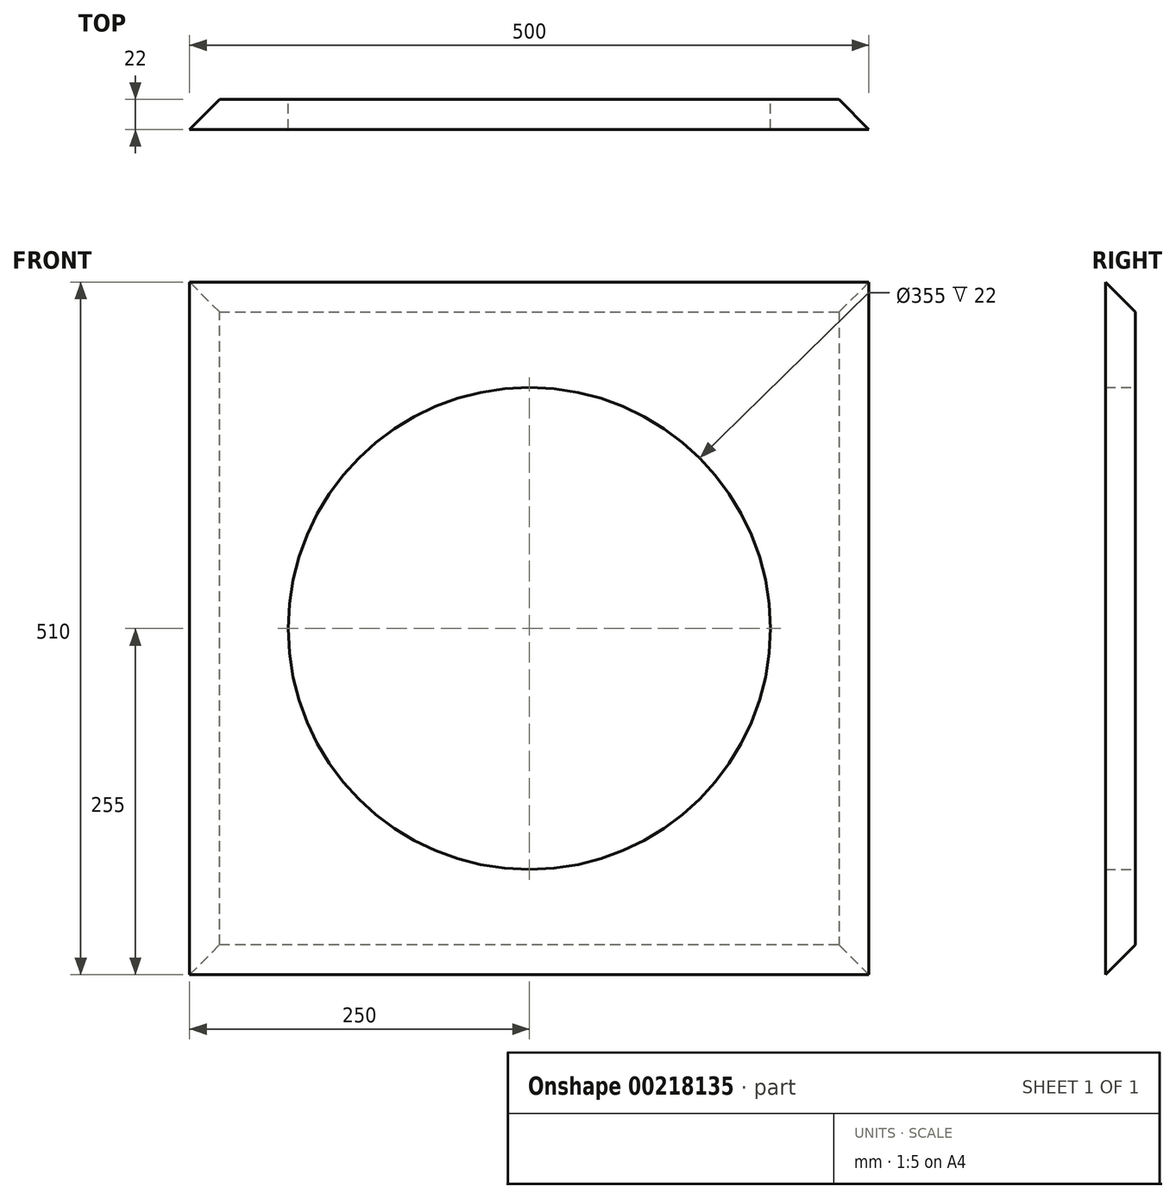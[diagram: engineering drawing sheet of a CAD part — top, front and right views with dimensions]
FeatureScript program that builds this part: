
annotation { "Feature Type Name" : "Feature", "Feature Type Description" : "" }
export const myFeature = defineFeature(function(context is Context, id is Id, definition is map)
    precondition{}
    {
        {
            var Q0;
            Q0=qCreatedBy(makeId("Front.planeOp"),FACE);
            var sketch = newSketch(context, id + "F0", { "sketchPlane" : qUnion([Q0])});
            skLineSegment(sketch, "E0.bottom", {"start": v(250, 255) * mm, "end": v(-250, 255) * mm});
            skLineSegment(sketch, "E0.top", {"start": v(250, -255) * mm, "end": v(-250, -255) * mm});
            skLineSegment(sketch, "E0.left", {"start": v(250, 255) * mm, "end": v(250, -255) * mm});
            skLineSegment(sketch, "E0.right", {"start": v(-250, 255) * mm, "end": v(-250, -255) * mm});
            skPoint(sketch, "E0.middle", {"position": v(0, 0) * mm});
            skLineSegment(sketch, "E1.bottom", {"start": v(161.5, 206.5) * mm, "end": v(-161.5, 206.5) * mm});
            skLineSegment(sketch, "E1.top", {"start": v(161.5, -206.5) * mm, "end": v(-161.5, -206.5) * mm});
            skLineSegment(sketch, "E1.left", {"start": v(201.5, 166.5) * mm, "end": v(201.5, -166.5) * mm});
            skLineSegment(sketch, "E1.right", {"start": v(-201.5, 166.5) * mm, "end": v(-201.5, -166.5) * mm});
            skPoint(sketch, "E2.visualSharp", {"position": v(-201.5, 206.5) * mm});
            skArc(sketch, "E2.filletArc", {"start": v(-161.5, 206.5) * mm, "mid": v(-189.78, 194.78) * mm, "end": v(-201.5, 166.5) * mm});
            skPoint(sketch, "E3.visualSharp", {"position": v(201.5, 206.5) * mm});
            skArc(sketch, "E3.filletArc", {"start": v(201.5, 166.5) * mm, "mid": v(189.78, 194.78) * mm, "end": v(161.5, 206.5) * mm});
            skPoint(sketch, "E4.visualSharp", {"position": v(201.5, -206.5) * mm});
            skArc(sketch, "E4.filletArc", {"start": v(161.5, -206.5) * mm, "mid": v(189.78, -194.78) * mm, "end": v(201.5, -166.5) * mm});
            skPoint(sketch, "E5.visualSharp", {"position": v(-201.5, -206.5) * mm});
            skArc(sketch, "E5.filletArc", {"start": v(-201.5, -166.5) * mm, "mid": v(-189.78, -194.78) * mm, "end": v(-161.5, -206.5) * mm});
            skCircle(sketch, "E6", {"center": v(0, 0) * mm, "radius": 177.5 * mm});
            skSolve(sketch);
        }
        {
            var Q0;
            Q0=makeQuery(id+"F0.imprint","IMPRINT",FACE,{"disambiguationData":[TD([[makeQuery(id+"F0.imprint","IMPRINT",EDGE,{"derivedFrom":sQuery(id+"F0.wireOp",EDGE,"E0.bottom")}),1.0]])]});
            var Q1;
            Q1=makeQuery(id+"F0.imprint","IMPRINT",FACE,{"disambiguationData":[TD([[makeQuery(id+"F0.imprint","IMPRINT",EDGE,{"derivedFrom":sQuery(id+"F0.wireOp",EDGE,"E1.bottom")}),1.0]])]});
            extrude(context, id + "F1", {"entities" : qUnion([Q0, Q1]), "depth" : 22 * mm});
        }
        {
            var Q0;
            Q0=makeQuery(id+"F1.opExtrude","CAP_EDGE",EDGE,{"disambiguationData":[OSD([sQuery(id+"F0.wireOp",EDGE,"E0.bottom")])],"isStart":true});
            var Q1;
            Q1=makeQuery(id+"F1.opExtrude","CAP_EDGE",EDGE,{"disambiguationData":[OSD([sQuery(id+"F0.wireOp",EDGE,"E0.left")])],"isStart":true});
            var Q2;
            Q2=makeQuery(id+"F1.opExtrude","CAP_EDGE",EDGE,{"disambiguationData":[OSD([sQuery(id+"F0.wireOp",EDGE,"E0.top")])],"isStart":true});
            var Q3;
            Q3=makeQuery(id+"F1.opExtrude","CAP_EDGE",EDGE,{"disambiguationData":[OSD([sQuery(id+"F0.wireOp",EDGE,"E0.right")])],"isStart":true});
            chamfer(context, id + "F2", {"entities" : qUnion([Q0, Q1, Q2, Q3]), "width" : 22 * mm, "tangentPropagation" : true});
        }
    });
